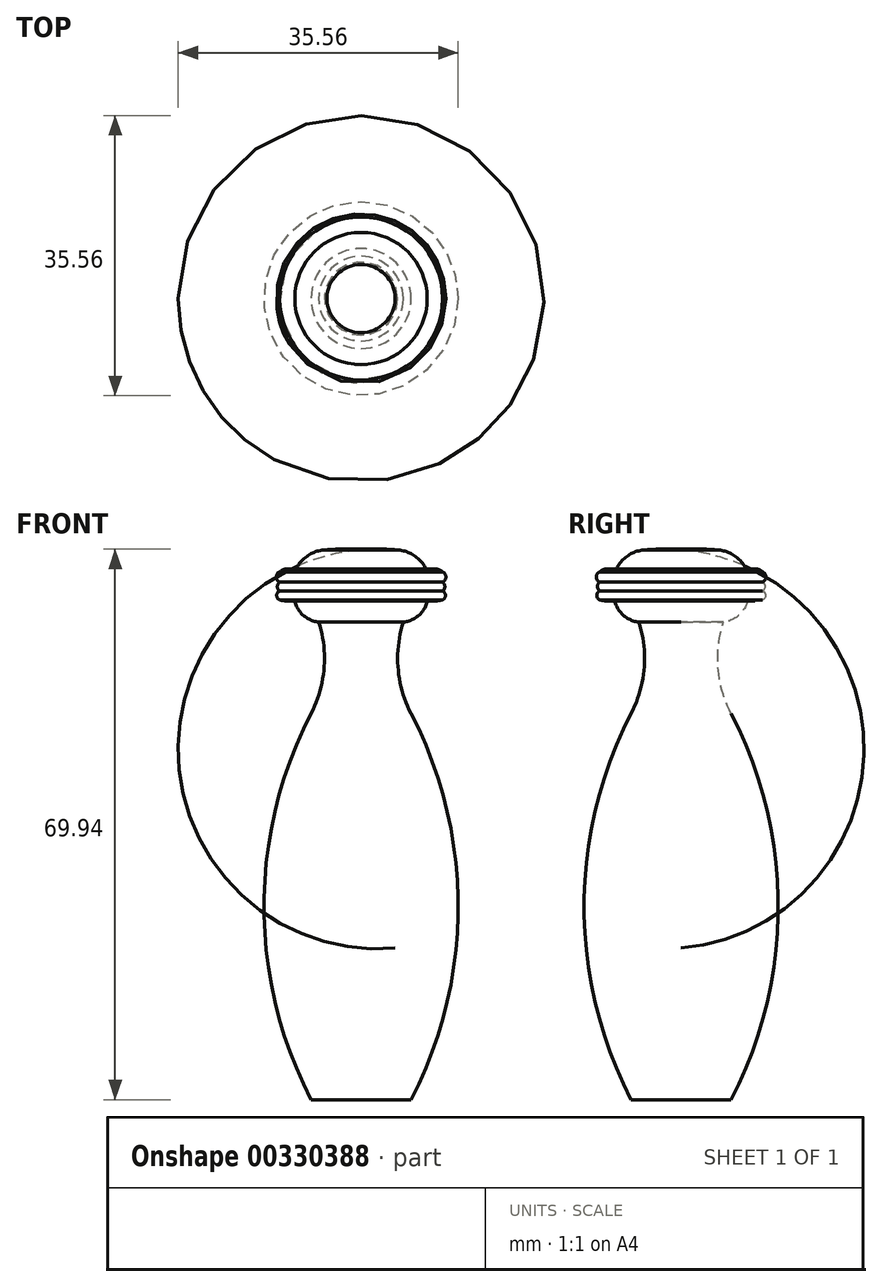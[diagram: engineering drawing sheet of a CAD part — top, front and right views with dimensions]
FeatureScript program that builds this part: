
annotation { "Feature Type Name" : "Feature", "Feature Type Description" : "" }
export const myFeature = defineFeature(function(context is Context, id is Id, definition is map)
    precondition{}
    {
        {
            var Q0;
            Q0=qCreatedBy(makeId("Front.planeOp"),FACE);
            var sketch = newSketch(context, id + "F0", { "sketchPlane" : qUnion([Q0])});
            skLineSegment(sketch, "E0", {"start": v(0, -69.85) * mm, "end": v(6.35, -69.85) * mm});
            skLineSegment(sketch, "E1", {"start": v(0, 0) * mm, "end": v(0, -69.85) * mm});
            skArc(sketch, "E2", {"start": v(6.35, -69.85) * mm, "mid": v(12.33, -45.32) * mm, "end": v(6.35, -20.8) * mm});
            skArc(sketch, "E3", {"start": v(4.32, 0) * mm, "mid": v(2.16, 0.1) * mm, "end": v(0, 0) * mm});
            skArc(sketch, "E4", {"start": v(5.37, -9.18) * mm, "mid": v(4.7, -15.09) * mm, "end": v(6.35, -20.8) * mm});
            skArc(sketch, "E5", {"start": v(5.37, -9.18) * mm, "mid": v(7.38, -8.28) * mm, "end": v(8.46, -6.36) * mm});
            skArc(sketch, "E6", {"start": v(8.46, -6.36) * mm, "mid": v(9.4, -6.49) * mm, "end": v(10.34, -6.36) * mm});
            skArc(sketch, "E7", {"start": v(10.34, -6.36) * mm, "mid": v(10.72, -5.8) * mm, "end": v(10.34, -5.23) * mm});
            skArc(sketch, "E8", {"start": v(10.34, -5.23) * mm, "mid": v(10.64, -4.67) * mm, "end": v(10.34, -4.1) * mm});
            skArc(sketch, "E9", {"start": v(10.34, -4.1) * mm, "mid": v(10.77, -3.45) * mm, "end": v(10.34, -2.8) * mm});
            skArc(sketch, "E10", {"start": v(10.34, -2.8) * mm, "mid": v(9.37, -2.41) * mm, "end": v(8.4, -2.8) * mm});
            skArc(sketch, "E11", {"start": v(8.4, -2.8) * mm, "mid": v(6.8, -0.76) * mm, "end": v(4.32, 0) * mm});
            skSolve(sketch);
        }
        {
            var Q0;
            Q0=makeQuery(id+"F0.imprint","IMPRINT",FACE,{"disambiguationData":[TD([[makeQuery(id+"F0.imprint","IMPRINT",EDGE,{"derivedFrom":sQuery(id+"F0.wireOp",EDGE,"E0")}),1.0]])]});
            var Q1;
            Q1=sQuery(id+"F0.wireOp",EDGE,"E1");
            revolve(context, id + "F1", {"entities" : qUnion([Q0]), "axis" : qUnion([Q1]), "revolveType" : RevolveType.FULL});
        }
    });
